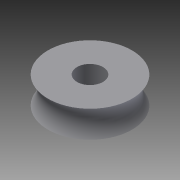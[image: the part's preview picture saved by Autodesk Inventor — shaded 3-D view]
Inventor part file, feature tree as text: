
AUTODESK INVENTOR PART (.ipt)
format: ipt  version: 2015 (Build 190159000, 159)  size: 123,392 bytes
history: native  units: in
note: dims shown in document units (in); Inventor stores cm internally (conversion verified against a paired STEP export)
features: sketch x3, extrude x2, revolve x1
ambient origin geometry x8: Origin, YZ Plane, XZ Plane, XY Plane, X Axis, Y Axis, Z Axis, Center Point
bodies: Solid1 (feature_tree)
feature tree (6):
  revolve  "Revolution1"  [1 undecoded]
  extrude  "Extrusion1"  Depth=0.5in
  extrude  "Extrusion2"  Depth=0.0551in
  sketch  "Sketch1"  dims[d0=90.0deg d1=0.32in]
  sketch  "Sketch2"  dims[d2=0.5in d3=0.4331in]
  sketch  "Sketch3"  dims[d4=0.0551in d5=0.0in d6=0.3091in d7=0.0551in d8=0.0in]
note: 1 required parameter value undecoded (feature->parameter linkage not recoverable at this tier; creation-order binding heuristic only, values carry confidence <= 0.55)
